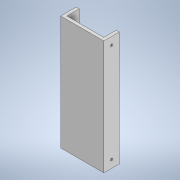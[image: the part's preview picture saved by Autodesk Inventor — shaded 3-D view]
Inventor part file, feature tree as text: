
AUTODESK INVENTOR PART (.ipt)
format: ipt  version: 2020 (Build 240168000, 168)  size: 137,728 bytes
history: native  units: mm
features: sketch x3, extrude x2, other x1, hole x1, mirror x1
ambient origin geometry x8: Origin, YZ Plane, XZ Plane, XY Plane, X Axis, Y Axis, Z Axis, Center Point
bodies: Body1 (feature_tree)
feature tree (8):
  other  "Твердое тело1"
  extrude  "Выдавливание1"  Depth=28.0mm
  extrude  "Выдавливание3"  Depth=10.0mm
  hole  "Отверстие1"  [1 undecoded]
  mirror  "Зеркальное отражение1"
  sketch  "Эскиз1"
  sketch  "Эскиз2"
  sketch  "Эскиз3"
note: 1 required parameter value undecoded (feature->parameter linkage not recoverable at this tier; creation-order binding heuristic only, values carry confidence <= 0.55)
